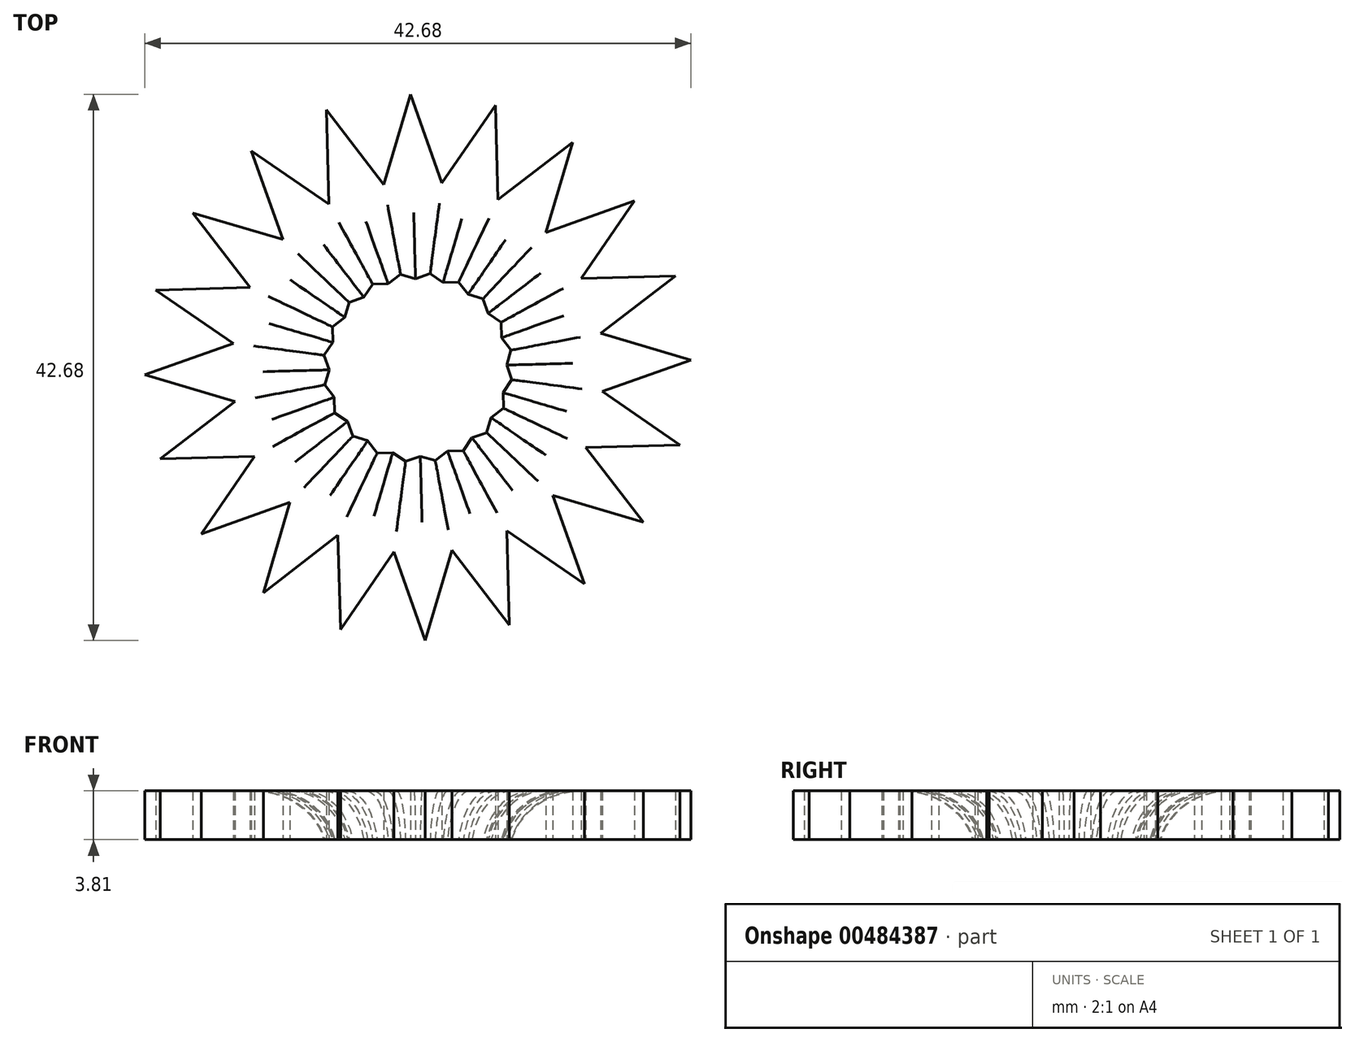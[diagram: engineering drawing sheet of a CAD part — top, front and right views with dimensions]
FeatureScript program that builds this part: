
annotation { "Feature Type Name" : "Feature", "Feature Type Description" : "" }
export const myFeature = defineFeature(function(context is Context, id is Id, definition is map)
    precondition{}
    {
        {
            var Q0;
            Q0=qCreatedBy(makeId("Top.planeOp"),FACE);
            var sketch = newSketch(context, id + "F0", { "sketchPlane" : qUnion([Q0])});
            skCircle(sketch, "E0.cCircle", {"center": v(0, 0) * mm, "radius": 21.09 * mm, "construction": true});
            skLineSegment(sketch, "E0.0", {"start": v(-20.48, 6.04) * mm, "end": v(-17.6, 12.08) * mm});
            skLineSegment(sketch, "E0.1", {"start": v(-17.6, 12.08) * mm, "end": v(-13.01, 16.93) * mm});
            skLineSegment(sketch, "E0.2", {"start": v(-13.01, 16.93) * mm, "end": v(-7.15, 20.12) * mm});
            skLineSegment(sketch, "E0.3", {"start": v(-7.15, 20.12) * mm, "end": v(-0.58, 21.34) * mm});
            skLineSegment(sketch, "E0.4", {"start": v(-0.58, 21.34) * mm, "end": v(6.04, 20.48) * mm});
            skLineSegment(sketch, "E0.5", {"start": v(6.04, 20.48) * mm, "end": v(12.08, 17.6) * mm});
            skLineSegment(sketch, "E0.6", {"start": v(12.08, 17.6) * mm, "end": v(16.93, 13.01) * mm});
            skLineSegment(sketch, "E0.7", {"start": v(16.93, 13.01) * mm, "end": v(20.12, 7.15) * mm});
            skLineSegment(sketch, "E0.8", {"start": v(20.12, 7.15) * mm, "end": v(21.34, 0.58) * mm});
            skLineSegment(sketch, "E0.9", {"start": v(21.34, 0.58) * mm, "end": v(20.48, -6.04) * mm});
            skLineSegment(sketch, "E0.10", {"start": v(20.48, -6.04) * mm, "end": v(17.6, -12.08) * mm});
            skLineSegment(sketch, "E0.11", {"start": v(17.6, -12.08) * mm, "end": v(13.01, -16.93) * mm});
            skLineSegment(sketch, "E0.12", {"start": v(13.01, -16.93) * mm, "end": v(7.15, -20.12) * mm});
            skLineSegment(sketch, "E0.13", {"start": v(7.15, -20.12) * mm, "end": v(0.58, -21.34) * mm});
            skLineSegment(sketch, "E0.14", {"start": v(0.58, -21.34) * mm, "end": v(-6.04, -20.48) * mm});
            skLineSegment(sketch, "E0.15", {"start": v(-6.04, -20.48) * mm, "end": v(-12.08, -17.6) * mm});
            skLineSegment(sketch, "E0.16", {"start": v(-12.08, -17.6) * mm, "end": v(-16.93, -13.01) * mm});
            skLineSegment(sketch, "E0.17", {"start": v(-16.93, -13.01) * mm, "end": v(-20.12, -7.15) * mm});
            skLineSegment(sketch, "E0.18", {"start": v(-20.12, -7.15) * mm, "end": v(-21.34, -0.58) * mm});
            skLineSegment(sketch, "E0.19", {"start": v(-21.34, -0.58) * mm, "end": v(-20.48, 6.04) * mm});
            skLineSegment(sketch, "E1", {"start": v(-12.08, -17.6) * mm, "end": v(-0.58, 21.34) * mm});
            skLineSegment(sketch, "E2", {"start": v(-0.58, 21.34) * mm, "end": v(13.01, -16.93) * mm});
            skLineSegment(sketch, "E3", {"start": v(13.01, -16.93) * mm, "end": v(-20.48, 6.04) * mm});
            skLineSegment(sketch, "E4", {"start": v(-16.93, -13.01) * mm, "end": v(6.04, 20.48) * mm});
            skLineSegment(sketch, "E5", {"start": v(6.04, 20.48) * mm, "end": v(7.15, -20.12) * mm});
            skLineSegment(sketch, "E6", {"start": v(7.15, -20.12) * mm, "end": v(-17.6, 12.08) * mm});
            skLineSegment(sketch, "E7", {"start": v(-17.6, 12.08) * mm, "end": v(21.34, 0.58) * mm});
            skLineSegment(sketch, "E8", {"start": v(21.34, 0.58) * mm, "end": v(-16.93, -13.01) * mm});
            skLineSegment(sketch, "E9", {"start": v(-20.48, 6.04) * mm, "end": v(20.12, 7.15) * mm});
            skLineSegment(sketch, "E10", {"start": v(20.12, 7.15) * mm, "end": v(-12.08, -17.6) * mm});
            skLineSegment(sketch, "E11", {"start": v(-20.12, -7.15) * mm, "end": v(12.08, 17.6) * mm});
            skLineSegment(sketch, "E12", {"start": v(-13.01, 16.93) * mm, "end": v(20.48, -6.04) * mm});
            skLineSegment(sketch, "E13", {"start": v(20.48, -6.04) * mm, "end": v(-20.12, -7.15) * mm});
            skLineSegment(sketch, "E14", {"start": v(-21.34, -0.58) * mm, "end": v(16.93, 13.01) * mm});
            skLineSegment(sketch, "E15", {"start": v(-7.15, 20.12) * mm, "end": v(17.6, -12.08) * mm});
            skLineSegment(sketch, "E16", {"start": v(17.6, -12.08) * mm, "end": v(-21.34, -0.58) * mm});
            skLineSegment(sketch, "E17", {"start": v(-6.04, -20.48) * mm, "end": v(16.93, 13.01) * mm});
            skLineSegment(sketch, "E18", {"start": v(0.58, -21.34) * mm, "end": v(-13.01, 16.93) * mm});
            skLineSegment(sketch, "E19", {"start": v(-6.04, -20.48) * mm, "end": v(-7.15, 20.12) * mm});
            skLineSegment(sketch, "E20", {"start": v(12.08, 17.6) * mm, "end": v(0.58, -21.34) * mm});
            skSolve(sketch);
        }
        {
            var Q0;
            {var subQ1=sQuery(id+"F0.wireOp",EDGE,"E1");var subQ3=sQuery(id+"F0.wireOp",EDGE,"E8");var subQ4=makeQuery(id+"F0.imprint","INTERSECT",VERTEX,{"derivedFrom":[subQ1,subQ3]});Q0=makeQuery(id+"F0.imprint","IMPRINT",FACE,{"disambiguationData":[TD([[makeQuery(id+"F0.imprint","IMPRINT",EDGE,{"disambiguationData":[TD([[subQ4,1.0]])],"derivedFrom":subQ3}),1.0]])]});}
            var Q1;
            {var subQ0=sQuery(id+"F0.wireOp",EDGE,"E8");var subQ1=sQuery(id+"F0.wireOp",EDGE,"E1");var subQ2=makeQuery(id+"F0.imprint","INTERSECT",VERTEX,{"derivedFrom":[subQ1,subQ0]});Q1=makeQuery(id+"F0.imprint","IMPRINT",FACE,{"disambiguationData":[TD([[makeQuery(id+"F0.imprint","IMPRINT",EDGE,{"disambiguationData":[TD([[subQ2,-1.0]])],"derivedFrom":subQ1}),1.0]])]});}
            var Q2;
            {var subQ0=sQuery(id+"F0.wireOp",EDGE,"E12");var subQ1=sQuery(id+"F0.wireOp",EDGE,"E1");var subQ2=makeQuery(id+"F0.imprint","INTERSECT",VERTEX,{"derivedFrom":[subQ1,subQ0]});Q2=makeQuery(id+"F0.imprint","IMPRINT",FACE,{"disambiguationData":[TD([[makeQuery(id+"F0.imprint","IMPRINT",EDGE,{"disambiguationData":[TD([[subQ2,-1.0]])],"derivedFrom":subQ1}),1.0]])]});}
            var Q3;
            {var subQ0=sQuery(id+"F0.wireOp",EDGE,"E2");var subQ5=sQuery(id+"F0.wireOp",EDGE,"E4");var subQ6=makeQuery(id+"F0.imprint","INTERSECT",VERTEX,{"derivedFrom":[subQ0,subQ5]});Q3=makeQuery(id+"F0.imprint","IMPRINT",FACE,{"disambiguationData":[TD([[makeQuery(id+"F0.imprint","IMPRINT",EDGE,{"disambiguationData":[TD([[subQ6,1.0]])],"derivedFrom":subQ5}),1.0]])]});}
            var Q4;
            {var subQ0=sQuery(id+"F0.wireOp",EDGE,"E4");var subQ1=sQuery(id+"F0.wireOp",EDGE,"E2");var subQ2=makeQuery(id+"F0.imprint","INTERSECT",VERTEX,{"derivedFrom":[subQ1,subQ0]});Q4=makeQuery(id+"F0.imprint","IMPRINT",FACE,{"disambiguationData":[TD([[makeQuery(id+"F0.imprint","IMPRINT",EDGE,{"disambiguationData":[TD([[subQ2,-1.0]])],"derivedFrom":subQ1}),1.0]])]});}
            var Q5;
            {var subQ0=sQuery(id+"F0.wireOp",EDGE,"E13");var subQ1=sQuery(id+"F0.wireOp",EDGE,"E2");var subQ2=makeQuery(id+"F0.imprint","INTERSECT",VERTEX,{"derivedFrom":[subQ1,subQ0]});Q5=makeQuery(id+"F0.imprint","IMPRINT",FACE,{"disambiguationData":[TD([[makeQuery(id+"F0.imprint","IMPRINT",EDGE,{"disambiguationData":[TD([[subQ2,-1.0]])],"derivedFrom":subQ1}),1.0]])]});}
            var Q6;
            {var subQ0=sQuery(id+"F0.wireOp",EDGE,"E3");var subQ5=sQuery(id+"F0.wireOp",EDGE,"E5");var subQ6=makeQuery(id+"F0.imprint","INTERSECT",VERTEX,{"derivedFrom":[subQ0,subQ5]});Q6=makeQuery(id+"F0.imprint","IMPRINT",FACE,{"disambiguationData":[TD([[makeQuery(id+"F0.imprint","IMPRINT",EDGE,{"disambiguationData":[TD([[subQ6,1.0]])],"derivedFrom":subQ5}),1.0]])]});}
            var Q7;
            {var subQ0=sQuery(id+"F0.wireOp",EDGE,"E5");var subQ1=sQuery(id+"F0.wireOp",EDGE,"E3");var subQ2=makeQuery(id+"F0.imprint","INTERSECT",VERTEX,{"derivedFrom":[subQ1,subQ0]});Q7=makeQuery(id+"F0.imprint","IMPRINT",FACE,{"disambiguationData":[TD([[makeQuery(id+"F0.imprint","IMPRINT",EDGE,{"disambiguationData":[TD([[subQ2,-1.0]])],"derivedFrom":subQ1}),1.0]])]});}
            var Q8;
            {var subQ0=sQuery(id+"F0.wireOp",EDGE,"E11");var subQ1=sQuery(id+"F0.wireOp",EDGE,"E3");var subQ2=makeQuery(id+"F0.imprint","INTERSECT",VERTEX,{"derivedFrom":[subQ1,subQ0]});Q8=makeQuery(id+"F0.imprint","IMPRINT",FACE,{"disambiguationData":[TD([[makeQuery(id+"F0.imprint","IMPRINT",EDGE,{"disambiguationData":[TD([[subQ2,-1.0]])],"derivedFrom":subQ1}),1.0]])]});}
            var Q9;
            {var subQ3=sQuery(id+"F0.wireOp",EDGE,"E14");var subQ5=sQuery(id+"F0.wireOp",EDGE,"E6");var subQ6=makeQuery(id+"F0.imprint","INTERSECT",VERTEX,{"derivedFrom":[subQ5,subQ3]});Q9=makeQuery(id+"F0.imprint","IMPRINT",FACE,{"disambiguationData":[TD([[makeQuery(id+"F0.imprint","IMPRINT",EDGE,{"disambiguationData":[TD([[subQ6,-1.0]])],"derivedFrom":subQ5}),1.0]])]});}
            var Q10;
            {var subQ0=sQuery(id+"F0.wireOp",EDGE,"E13");var subQ1=sQuery(id+"F0.wireOp",EDGE,"E4");var subQ2=makeQuery(id+"F0.imprint","INTERSECT",VERTEX,{"derivedFrom":[subQ1,subQ0]});Q10=makeQuery(id+"F0.imprint","IMPRINT",FACE,{"disambiguationData":[TD([[makeQuery(id+"F0.imprint","IMPRINT",EDGE,{"disambiguationData":[TD([[subQ2,-1.0]])],"derivedFrom":subQ1}),1.0]])]});}
            var Q11;
            {var subQ0=sQuery(id+"F0.wireOp",EDGE,"E11");var subQ1=sQuery(id+"F0.wireOp",EDGE,"E5");var subQ2=makeQuery(id+"F0.imprint","INTERSECT",VERTEX,{"derivedFrom":[subQ1,subQ0]});Q11=makeQuery(id+"F0.imprint","IMPRINT",FACE,{"disambiguationData":[TD([[makeQuery(id+"F0.imprint","IMPRINT",EDGE,{"disambiguationData":[TD([[subQ2,-1.0]])],"derivedFrom":subQ1}),1.0]])]});}
            var Q12;
            {var subQ0=sQuery(id+"F0.wireOp",EDGE,"E20");var subQ1=sQuery(id+"F0.wireOp",EDGE,"E6");var subQ2=makeQuery(id+"F0.imprint","INTERSECT",VERTEX,{"derivedFrom":[subQ1,subQ0]});Q12=makeQuery(id+"F0.imprint","IMPRINT",FACE,{"disambiguationData":[TD([[makeQuery(id+"F0.imprint","IMPRINT",EDGE,{"disambiguationData":[TD([[subQ2,-1.0]])],"derivedFrom":subQ1}),1.0]])]});}
            var Q13;
            {var subQ1=sQuery(id+"F0.wireOp",EDGE,"E6");var subQ3=sQuery(id+"F0.wireOp",EDGE,"E9");var subQ4=makeQuery(id+"F0.imprint","INTERSECT",VERTEX,{"derivedFrom":[subQ1,subQ3]});Q13=makeQuery(id+"F0.imprint","IMPRINT",FACE,{"disambiguationData":[TD([[makeQuery(id+"F0.imprint","IMPRINT",EDGE,{"disambiguationData":[TD([[subQ4,-1.0]])],"derivedFrom":subQ3}),1.0]])]});}
            var Q14;
            {var subQ0=sQuery(id+"F0.wireOp",EDGE,"E18");var subQ1=sQuery(id+"F0.wireOp",EDGE,"E7");var subQ2=makeQuery(id+"F0.imprint","INTERSECT",VERTEX,{"derivedFrom":[subQ1,subQ0]});Q14=makeQuery(id+"F0.imprint","IMPRINT",FACE,{"disambiguationData":[TD([[makeQuery(id+"F0.imprint","IMPRINT",EDGE,{"disambiguationData":[TD([[subQ2,-1.0]])],"derivedFrom":subQ1}),1.0]])]});}
            var Q15;
            {var subQ0=sQuery(id+"F0.wireOp",EDGE,"E17");var subQ1=sQuery(id+"F0.wireOp",EDGE,"E7");var subQ2=makeQuery(id+"F0.imprint","INTERSECT",VERTEX,{"derivedFrom":[subQ1,subQ0]});Q15=makeQuery(id+"F0.imprint","IMPRINT",FACE,{"disambiguationData":[TD([[makeQuery(id+"F0.imprint","IMPRINT",EDGE,{"disambiguationData":[TD([[subQ2,-1.0]])],"derivedFrom":subQ1}),1.0]])]});}
            var Q16;
            {var subQ1=sQuery(id+"F0.wireOp",EDGE,"E7");var subQ3=sQuery(id+"F0.wireOp",EDGE,"E10");var subQ4=makeQuery(id+"F0.imprint","INTERSECT",VERTEX,{"derivedFrom":[subQ1,subQ3]});Q16=makeQuery(id+"F0.imprint","IMPRINT",FACE,{"disambiguationData":[TD([[makeQuery(id+"F0.imprint","IMPRINT",EDGE,{"disambiguationData":[TD([[subQ4,-1.0]])],"derivedFrom":subQ3}),1.0]])]});}
            var Q17;
            {var subQ0=sQuery(id+"F0.wireOp",EDGE,"E12");var subQ1=sQuery(id+"F0.wireOp",EDGE,"E8");var subQ2=makeQuery(id+"F0.imprint","INTERSECT",VERTEX,{"derivedFrom":[subQ1,subQ0]});Q17=makeQuery(id+"F0.imprint","IMPRINT",FACE,{"disambiguationData":[TD([[makeQuery(id+"F0.imprint","IMPRINT",EDGE,{"disambiguationData":[TD([[subQ2,-1.0]])],"derivedFrom":subQ1}),1.0]])]});}
            var Q18;
            {var subQ0=sQuery(id+"F0.wireOp",EDGE,"E20");var subQ1=sQuery(id+"F0.wireOp",EDGE,"E9");var subQ2=makeQuery(id+"F0.imprint","INTERSECT",VERTEX,{"derivedFrom":[subQ1,subQ0]});Q18=makeQuery(id+"F0.imprint","IMPRINT",FACE,{"disambiguationData":[TD([[makeQuery(id+"F0.imprint","IMPRINT",EDGE,{"disambiguationData":[TD([[subQ2,-1.0]])],"derivedFrom":subQ1}),1.0]])]});}
            var Q19;
            {var subQ0=sQuery(id+"F0.wireOp",EDGE,"E18");var subQ1=sQuery(id+"F0.wireOp",EDGE,"E10");var subQ2=makeQuery(id+"F0.imprint","INTERSECT",VERTEX,{"derivedFrom":[subQ1,subQ0]});Q19=makeQuery(id+"F0.imprint","IMPRINT",FACE,{"disambiguationData":[TD([[makeQuery(id+"F0.imprint","IMPRINT",EDGE,{"disambiguationData":[TD([[subQ2,-1.0]])],"derivedFrom":subQ1}),1.0]])]});}
            var Q20;
            {var subQ0=sQuery(id+"F0.wireOp",EDGE,"E13");var subQ1=sQuery(id+"F0.wireOp",EDGE,"E1");var subQ2=makeQuery(id+"F0.imprint","INTERSECT",VERTEX,{"derivedFrom":[subQ1,subQ0]});Q20=makeQuery(id+"F0.imprint","IMPRINT",FACE,{"disambiguationData":[TD([[makeQuery(id+"F0.imprint","IMPRINT",EDGE,{"disambiguationData":[TD([[subQ2,-1.0]])],"derivedFrom":subQ1}),1.0]])]});}
            var Q21;
            {var subQ0=sQuery(id+"F0.wireOp",EDGE,"E8");var subQ1=sQuery(id+"F0.wireOp",EDGE,"E1");var subQ2=makeQuery(id+"F0.imprint","INTERSECT",VERTEX,{"derivedFrom":[subQ1,subQ0]});Q21=makeQuery(id+"F0.imprint","IMPRINT",FACE,{"disambiguationData":[TD([[makeQuery(id+"F0.imprint","IMPRINT",EDGE,{"disambiguationData":[TD([[subQ2,-1.0]])],"derivedFrom":subQ1}),-1.0]])]});}
            var Q22;
            {var subQ0=sQuery(id+"F0.wireOp",EDGE,"E18");var subQ1=sQuery(id+"F0.wireOp",EDGE,"E8");var subQ2=makeQuery(id+"F0.imprint","INTERSECT",VERTEX,{"derivedFrom":[subQ1,subQ0]});Q22=makeQuery(id+"F0.imprint","IMPRINT",FACE,{"disambiguationData":[TD([[makeQuery(id+"F0.imprint","IMPRINT",EDGE,{"disambiguationData":[TD([[subQ2,-1.0]])],"derivedFrom":subQ1}),1.0]])]});}
            var Q23;
            {var subQ0=sQuery(id+"F0.wireOp",EDGE,"E17");var subQ1=sQuery(id+"F0.wireOp",EDGE,"E6");var subQ2=makeQuery(id+"F0.imprint","INTERSECT",VERTEX,{"derivedFrom":[subQ1,subQ0]});Q23=makeQuery(id+"F0.imprint","IMPRINT",FACE,{"disambiguationData":[TD([[makeQuery(id+"F0.imprint","IMPRINT",EDGE,{"disambiguationData":[TD([[subQ2,-1.0]])],"derivedFrom":subQ1}),1.0]])]});}
            var Q24;
            {var subQ0=sQuery(id+"F0.wireOp",EDGE,"E20");var subQ1=sQuery(id+"F0.wireOp",EDGE,"E3");var subQ2=makeQuery(id+"F0.imprint","INTERSECT",VERTEX,{"derivedFrom":[subQ1,subQ0]});Q24=makeQuery(id+"F0.imprint","IMPRINT",FACE,{"disambiguationData":[TD([[makeQuery(id+"F0.imprint","IMPRINT",EDGE,{"disambiguationData":[TD([[subQ2,-1.0]])],"derivedFrom":subQ1}),1.0]])]});}
            var Q25;
            {var subQ0=sQuery(id+"F0.wireOp",EDGE,"E5");var subQ1=sQuery(id+"F0.wireOp",EDGE,"E3");var subQ2=makeQuery(id+"F0.imprint","INTERSECT",VERTEX,{"derivedFrom":[subQ1,subQ0]});Q25=makeQuery(id+"F0.imprint","IMPRINT",FACE,{"disambiguationData":[TD([[makeQuery(id+"F0.imprint","IMPRINT",EDGE,{"disambiguationData":[TD([[subQ2,-1.0]])],"derivedFrom":subQ1}),-1.0]])]});}
            var Q26;
            {var subQ0=sQuery(id+"F0.wireOp",EDGE,"E13");var subQ1=sQuery(id+"F0.wireOp",EDGE,"E2");var subQ2=makeQuery(id+"F0.imprint","INTERSECT",VERTEX,{"derivedFrom":[subQ1,subQ0]});Q26=makeQuery(id+"F0.imprint","IMPRINT",FACE,{"disambiguationData":[TD([[makeQuery(id+"F0.imprint","IMPRINT",EDGE,{"disambiguationData":[TD([[subQ2,-1.0]])],"derivedFrom":subQ1}),-1.0]])]});}
            var Q27;
            {var subQ0=sQuery(id+"F0.wireOp",EDGE,"E8");var subQ1=sQuery(id+"F0.wireOp",EDGE,"E2");var subQ2=makeQuery(id+"F0.imprint","INTERSECT",VERTEX,{"derivedFrom":[subQ1,subQ0]});Q27=makeQuery(id+"F0.imprint","IMPRINT",FACE,{"disambiguationData":[TD([[makeQuery(id+"F0.imprint","IMPRINT",EDGE,{"disambiguationData":[TD([[subQ2,-1.0]])],"derivedFrom":subQ1}),1.0]])]});}
            var Q28;
            {var subQ0=sQuery(id+"F0.wireOp",EDGE,"E12");var subQ1=sQuery(id+"F0.wireOp",EDGE,"E8");var subQ2=makeQuery(id+"F0.imprint","INTERSECT",VERTEX,{"derivedFrom":[subQ1,subQ0]});Q28=makeQuery(id+"F0.imprint","IMPRINT",FACE,{"disambiguationData":[TD([[makeQuery(id+"F0.imprint","IMPRINT",EDGE,{"disambiguationData":[TD([[subQ2,-1.0]])],"derivedFrom":subQ1}),-1.0]])]});}
            var Q29;
            {var subQ0=sQuery(id+"F0.wireOp",EDGE,"E17");var subQ1=sQuery(id+"F0.wireOp",EDGE,"E7");var subQ2=makeQuery(id+"F0.imprint","INTERSECT",VERTEX,{"derivedFrom":[subQ1,subQ0]});Q29=makeQuery(id+"F0.imprint","IMPRINT",FACE,{"disambiguationData":[TD([[makeQuery(id+"F0.imprint","IMPRINT",EDGE,{"disambiguationData":[TD([[subQ2,-1.0]])],"derivedFrom":subQ1}),-1.0]])]});}
            var Q30;
            {var subQ0=sQuery(id+"F0.wireOp",EDGE,"E20");var subQ1=sQuery(id+"F0.wireOp",EDGE,"E7");var subQ2=makeQuery(id+"F0.imprint","INTERSECT",VERTEX,{"derivedFrom":[subQ1,subQ0]});Q30=makeQuery(id+"F0.imprint","IMPRINT",FACE,{"disambiguationData":[TD([[makeQuery(id+"F0.imprint","IMPRINT",EDGE,{"disambiguationData":[TD([[subQ2,-1.0]])],"derivedFrom":subQ1}),1.0]])]});}
            var Q31;
            {var subQ0=sQuery(id+"F0.wireOp",EDGE,"E14");var subQ1=sQuery(id+"F0.wireOp",EDGE,"E5");var subQ2=makeQuery(id+"F0.imprint","INTERSECT",VERTEX,{"derivedFrom":[subQ1,subQ0]});Q31=makeQuery(id+"F0.imprint","IMPRINT",FACE,{"disambiguationData":[TD([[makeQuery(id+"F0.imprint","IMPRINT",EDGE,{"disambiguationData":[TD([[subQ2,-1.0]])],"derivedFrom":subQ1}),1.0]])]});}
            var Q32;
            {var subQ0=sQuery(id+"F0.wireOp",EDGE,"E11");var subQ1=sQuery(id+"F0.wireOp",EDGE,"E2");var subQ2=makeQuery(id+"F0.imprint","INTERSECT",VERTEX,{"derivedFrom":[subQ1,subQ0]});Q32=makeQuery(id+"F0.imprint","IMPRINT",FACE,{"disambiguationData":[TD([[makeQuery(id+"F0.imprint","IMPRINT",EDGE,{"disambiguationData":[TD([[subQ2,-1.0]])],"derivedFrom":subQ1}),1.0]])]});}
            var Q33;
            {var subQ0=sQuery(id+"F0.wireOp",EDGE,"E4");var subQ1=sQuery(id+"F0.wireOp",EDGE,"E2");var subQ2=makeQuery(id+"F0.imprint","INTERSECT",VERTEX,{"derivedFrom":[subQ1,subQ0]});Q33=makeQuery(id+"F0.imprint","IMPRINT",FACE,{"disambiguationData":[TD([[makeQuery(id+"F0.imprint","IMPRINT",EDGE,{"disambiguationData":[TD([[subQ2,-1.0]])],"derivedFrom":subQ1}),-1.0]])]});}
            var Q34;
            {var subQ0=sQuery(id+"F0.wireOp",EDGE,"E12");var subQ1=sQuery(id+"F0.wireOp",EDGE,"E1");var subQ2=makeQuery(id+"F0.imprint","INTERSECT",VERTEX,{"derivedFrom":[subQ1,subQ0]});Q34=makeQuery(id+"F0.imprint","IMPRINT",FACE,{"disambiguationData":[TD([[makeQuery(id+"F0.imprint","IMPRINT",EDGE,{"disambiguationData":[TD([[subQ2,-1.0]])],"derivedFrom":subQ1}),-1.0]])]});}
            var Q35;
            {var subQ0=sQuery(id+"F0.wireOp",EDGE,"E7");var subQ1=sQuery(id+"F0.wireOp",EDGE,"E1");var subQ2=makeQuery(id+"F0.imprint","INTERSECT",VERTEX,{"derivedFrom":[subQ1,subQ0]});Q35=makeQuery(id+"F0.imprint","IMPRINT",FACE,{"disambiguationData":[TD([[makeQuery(id+"F0.imprint","IMPRINT",EDGE,{"disambiguationData":[TD([[subQ2,-1.0]])],"derivedFrom":subQ1}),1.0]])]});}
            var Q36;
            {var subQ0=sQuery(id+"F0.wireOp",EDGE,"E18");var subQ1=sQuery(id+"F0.wireOp",EDGE,"E7");var subQ2=makeQuery(id+"F0.imprint","INTERSECT",VERTEX,{"derivedFrom":[subQ1,subQ0]});Q36=makeQuery(id+"F0.imprint","IMPRINT",FACE,{"disambiguationData":[TD([[makeQuery(id+"F0.imprint","IMPRINT",EDGE,{"disambiguationData":[TD([[subQ2,-1.0]])],"derivedFrom":subQ1}),-1.0]])]});}
            var Q37;
            {var subQ0=sQuery(id+"F0.wireOp",EDGE,"E14");var subQ1=sQuery(id+"F0.wireOp",EDGE,"E6");var subQ2=makeQuery(id+"F0.imprint","INTERSECT",VERTEX,{"derivedFrom":[subQ1,subQ0]});Q37=makeQuery(id+"F0.imprint","IMPRINT",FACE,{"disambiguationData":[TD([[makeQuery(id+"F0.imprint","IMPRINT",EDGE,{"disambiguationData":[TD([[subQ2,-1.0]])],"derivedFrom":subQ1}),-1.0]])]});}
            var Q38;
            {var subQ0=sQuery(id+"F0.wireOp",EDGE,"E11");var subQ1=sQuery(id+"F0.wireOp",EDGE,"E3");var subQ2=makeQuery(id+"F0.imprint","INTERSECT",VERTEX,{"derivedFrom":[subQ1,subQ0]});Q38=makeQuery(id+"F0.imprint","IMPRINT",FACE,{"disambiguationData":[TD([[makeQuery(id+"F0.imprint","IMPRINT",EDGE,{"disambiguationData":[TD([[subQ2,-1.0]])],"derivedFrom":subQ1}),-1.0]])]});}
            var Q39;
            {var subQ0=sQuery(id+"F0.wireOp",EDGE,"E4");var subQ1=sQuery(id+"F0.wireOp",EDGE,"E3");var subQ2=makeQuery(id+"F0.imprint","INTERSECT",VERTEX,{"derivedFrom":[subQ1,subQ0]});Q39=makeQuery(id+"F0.imprint","IMPRINT",FACE,{"disambiguationData":[TD([[makeQuery(id+"F0.imprint","IMPRINT",EDGE,{"disambiguationData":[TD([[subQ2,-1.0]])],"derivedFrom":subQ1}),1.0]])]});}
            var Q40;
            {var subQ0=sQuery(id+"F0.wireOp",EDGE,"E10");var subQ1=sQuery(id+"F0.wireOp",EDGE,"E2");var subQ2=makeQuery(id+"F0.imprint","INTERSECT",VERTEX,{"derivedFrom":[subQ1,subQ0]});Q40=makeQuery(id+"F0.imprint","IMPRINT",FACE,{"disambiguationData":[TD([[makeQuery(id+"F0.imprint","IMPRINT",EDGE,{"disambiguationData":[TD([[subQ2,-1.0]])],"derivedFrom":subQ1}),1.0]])]});}
            var Q41;
            {var subQ0=sQuery(id+"F0.wireOp",EDGE,"E12");var subQ1=sQuery(id+"F0.wireOp",EDGE,"E10");var subQ2=makeQuery(id+"F0.imprint","INTERSECT",VERTEX,{"derivedFrom":[subQ1,subQ0]});Q41=makeQuery(id+"F0.imprint","IMPRINT",FACE,{"disambiguationData":[TD([[makeQuery(id+"F0.imprint","IMPRINT",EDGE,{"disambiguationData":[TD([[subQ2,-1.0]])],"derivedFrom":subQ1}),-1.0]])]});}
            var Q42;
            {var subQ0=sQuery(id+"F0.wireOp",EDGE,"E20");var subQ1=sQuery(id+"F0.wireOp",EDGE,"E7");var subQ2=makeQuery(id+"F0.imprint","INTERSECT",VERTEX,{"derivedFrom":[subQ1,subQ0]});Q42=makeQuery(id+"F0.imprint","IMPRINT",FACE,{"disambiguationData":[TD([[makeQuery(id+"F0.imprint","IMPRINT",EDGE,{"disambiguationData":[TD([[subQ2,-1.0]])],"derivedFrom":subQ1}),-1.0]])]});}
            var Q43;
            {var subQ0=sQuery(id+"F0.wireOp",EDGE,"E11");var subQ1=sQuery(id+"F0.wireOp",EDGE,"E2");var subQ2=makeQuery(id+"F0.imprint","INTERSECT",VERTEX,{"derivedFrom":[subQ1,subQ0]});Q43=makeQuery(id+"F0.imprint","IMPRINT",FACE,{"disambiguationData":[TD([[makeQuery(id+"F0.imprint","IMPRINT",EDGE,{"disambiguationData":[TD([[subQ2,-1.0]])],"derivedFrom":subQ1}),-1.0]])]});}
            var Q44;
            {var subQ0=sQuery(id+"F0.wireOp",EDGE,"E12");var subQ1=sQuery(id+"F0.wireOp",EDGE,"E4");var subQ2=makeQuery(id+"F0.imprint","INTERSECT",VERTEX,{"derivedFrom":[subQ1,subQ0]});Q44=makeQuery(id+"F0.imprint","IMPRINT",FACE,{"disambiguationData":[TD([[makeQuery(id+"F0.imprint","IMPRINT",EDGE,{"disambiguationData":[TD([[subQ2,-1.0]])],"derivedFrom":subQ1}),-1.0]])]});}
            var Q45;
            {var subQ0=sQuery(id+"F0.wireOp",EDGE,"E7");var subQ1=sQuery(id+"F0.wireOp",EDGE,"E1");var subQ2=makeQuery(id+"F0.imprint","INTERSECT",VERTEX,{"derivedFrom":[subQ1,subQ0]});Q45=makeQuery(id+"F0.imprint","IMPRINT",FACE,{"disambiguationData":[TD([[makeQuery(id+"F0.imprint","IMPRINT",EDGE,{"disambiguationData":[TD([[subQ2,-1.0]])],"derivedFrom":subQ1}),-1.0]])]});}
            var Q46;
            {var subQ0=sQuery(id+"F0.wireOp",EDGE,"E9");var subQ1=sQuery(id+"F0.wireOp",EDGE,"E1");var subQ2=makeQuery(id+"F0.imprint","INTERSECT",VERTEX,{"derivedFrom":[subQ1,subQ0]});Q46=makeQuery(id+"F0.imprint","IMPRINT",FACE,{"disambiguationData":[TD([[makeQuery(id+"F0.imprint","IMPRINT",EDGE,{"disambiguationData":[TD([[subQ2,-1.0]])],"derivedFrom":subQ1}),1.0]])]});}
            var Q47;
            {var subQ0=sQuery(id+"F0.wireOp",EDGE,"E18");var subQ1=sQuery(id+"F0.wireOp",EDGE,"E9");var subQ2=makeQuery(id+"F0.imprint","INTERSECT",VERTEX,{"derivedFrom":[subQ1,subQ0]});Q47=makeQuery(id+"F0.imprint","IMPRINT",FACE,{"disambiguationData":[TD([[makeQuery(id+"F0.imprint","IMPRINT",EDGE,{"disambiguationData":[TD([[subQ2,-1.0]])],"derivedFrom":subQ1}),-1.0]])]});}
            var Q48;
            {var subQ0=sQuery(id+"F0.wireOp",EDGE,"E11");var subQ1=sQuery(id+"F0.wireOp",EDGE,"E6");var subQ2=makeQuery(id+"F0.imprint","INTERSECT",VERTEX,{"derivedFrom":[subQ1,subQ0]});Q48=makeQuery(id+"F0.imprint","IMPRINT",FACE,{"disambiguationData":[TD([[makeQuery(id+"F0.imprint","IMPRINT",EDGE,{"disambiguationData":[TD([[subQ2,-1.0]])],"derivedFrom":subQ1}),-1.0]])]});}
            var Q49;
            {var subQ0=sQuery(id+"F0.wireOp",EDGE,"E4");var subQ1=sQuery(id+"F0.wireOp",EDGE,"E3");var subQ2=makeQuery(id+"F0.imprint","INTERSECT",VERTEX,{"derivedFrom":[subQ1,subQ0]});Q49=makeQuery(id+"F0.imprint","IMPRINT",FACE,{"disambiguationData":[TD([[makeQuery(id+"F0.imprint","IMPRINT",EDGE,{"disambiguationData":[TD([[subQ2,-1.0]])],"derivedFrom":subQ1}),-1.0]])]});}
            var Q50;
            {var subQ0=sQuery(id+"F0.wireOp",EDGE,"E16");var subQ1=sQuery(id+"F0.wireOp",EDGE,"E1");var subQ2=makeQuery(id+"F0.imprint","INTERSECT",VERTEX,{"derivedFrom":[subQ1,subQ0]});Q50=makeQuery(id+"F0.imprint","IMPRINT",FACE,{"disambiguationData":[TD([[makeQuery(id+"F0.imprint","IMPRINT",EDGE,{"disambiguationData":[TD([[subQ2,-1.0]])],"derivedFrom":subQ1}),1.0]])]});}
            var Q51;
            {var subQ0=sQuery(id+"F0.wireOp",EDGE,"E13");var subQ1=sQuery(id+"F0.wireOp",EDGE,"E1");var subQ2=makeQuery(id+"F0.imprint","INTERSECT",VERTEX,{"derivedFrom":[subQ1,subQ0]});Q51=makeQuery(id+"F0.imprint","IMPRINT",FACE,{"disambiguationData":[TD([[makeQuery(id+"F0.imprint","IMPRINT",EDGE,{"disambiguationData":[TD([[subQ2,-1.0]])],"derivedFrom":subQ1}),-1.0]])]});}
            var Q52;
            {var subQ0=sQuery(id+"F0.wireOp",EDGE,"E18");var subQ1=sQuery(id+"F0.wireOp",EDGE,"E8");var subQ2=makeQuery(id+"F0.imprint","INTERSECT",VERTEX,{"derivedFrom":[subQ1,subQ0]});Q52=makeQuery(id+"F0.imprint","IMPRINT",FACE,{"disambiguationData":[TD([[makeQuery(id+"F0.imprint","IMPRINT",EDGE,{"disambiguationData":[TD([[subQ2,-1.0]])],"derivedFrom":subQ1}),-1.0]])]});}
            var Q53;
            {var subQ0=sQuery(id+"F0.wireOp",EDGE,"E10");var subQ1=sQuery(id+"F0.wireOp",EDGE,"E6");var subQ2=makeQuery(id+"F0.imprint","INTERSECT",VERTEX,{"derivedFrom":[subQ1,subQ0]});Q53=makeQuery(id+"F0.imprint","IMPRINT",FACE,{"disambiguationData":[TD([[makeQuery(id+"F0.imprint","IMPRINT",EDGE,{"disambiguationData":[TD([[subQ2,-1.0]])],"derivedFrom":subQ1}),1.0]])]});}
            var Q54;
            {var subQ0=sQuery(id+"F0.wireOp",EDGE,"E17");var subQ1=sQuery(id+"F0.wireOp",EDGE,"E3");var subQ2=makeQuery(id+"F0.imprint","INTERSECT",VERTEX,{"derivedFrom":[subQ1,subQ0]});Q54=makeQuery(id+"F0.imprint","IMPRINT",FACE,{"disambiguationData":[TD([[makeQuery(id+"F0.imprint","IMPRINT",EDGE,{"disambiguationData":[TD([[subQ2,-1.0]])],"derivedFrom":subQ1}),1.0]])]});}
            var Q55;
            {var subQ0=sQuery(id+"F0.wireOp",EDGE,"E20");var subQ1=sQuery(id+"F0.wireOp",EDGE,"E3");var subQ2=makeQuery(id+"F0.imprint","INTERSECT",VERTEX,{"derivedFrom":[subQ1,subQ0]});Q55=makeQuery(id+"F0.imprint","IMPRINT",FACE,{"disambiguationData":[TD([[makeQuery(id+"F0.imprint","IMPRINT",EDGE,{"disambiguationData":[TD([[subQ2,-1.0]])],"derivedFrom":subQ1}),-1.0]])]});}
            var Q56;
            {var subQ0=sQuery(id+"F0.wireOp",EDGE,"E13");var subQ1=sQuery(id+"F0.wireOp",EDGE,"E5");var subQ2=makeQuery(id+"F0.imprint","INTERSECT",VERTEX,{"derivedFrom":[subQ1,subQ0]});Q56=makeQuery(id+"F0.imprint","IMPRINT",FACE,{"disambiguationData":[TD([[makeQuery(id+"F0.imprint","IMPRINT",EDGE,{"disambiguationData":[TD([[subQ2,-1.0]])],"derivedFrom":subQ1}),-1.0]])]});}
            var Q57;
            {var subQ0=sQuery(id+"F0.wireOp",EDGE,"E8");var subQ1=sQuery(id+"F0.wireOp",EDGE,"E2");var subQ2=makeQuery(id+"F0.imprint","INTERSECT",VERTEX,{"derivedFrom":[subQ1,subQ0]});Q57=makeQuery(id+"F0.imprint","IMPRINT",FACE,{"disambiguationData":[TD([[makeQuery(id+"F0.imprint","IMPRINT",EDGE,{"disambiguationData":[TD([[subQ2,-1.0]])],"derivedFrom":subQ1}),-1.0]])]});}
            var Q58;
            {var subQ0=sQuery(id+"F0.wireOp",EDGE,"E10");var subQ1=sQuery(id+"F0.wireOp",EDGE,"E2");var subQ2=makeQuery(id+"F0.imprint","INTERSECT",VERTEX,{"derivedFrom":[subQ1,subQ0]});Q58=makeQuery(id+"F0.imprint","IMPRINT",FACE,{"disambiguationData":[TD([[makeQuery(id+"F0.imprint","IMPRINT",EDGE,{"disambiguationData":[TD([[subQ2,-1.0]])],"derivedFrom":subQ1}),-1.0]])]});}
            var Q59;
            {var subQ0=sQuery(id+"F0.wireOp",EDGE,"E17");var subQ1=sQuery(id+"F0.wireOp",EDGE,"E2");var subQ2=makeQuery(id+"F0.imprint","INTERSECT",VERTEX,{"derivedFrom":[subQ1,subQ0]});Q59=makeQuery(id+"F0.imprint","IMPRINT",FACE,{"disambiguationData":[TD([[makeQuery(id+"F0.imprint","IMPRINT",EDGE,{"disambiguationData":[TD([[subQ2,-1.0]])],"derivedFrom":subQ1}),1.0]])]});}
            var Q60;
            {var subQ0=sQuery(id+"F0.wireOp",EDGE,"E20");var subQ1=sQuery(id+"F0.wireOp",EDGE,"E12");var subQ2=makeQuery(id+"F0.imprint","INTERSECT",VERTEX,{"derivedFrom":[subQ1,subQ0]});Q60=makeQuery(id+"F0.imprint","IMPRINT",FACE,{"disambiguationData":[TD([[makeQuery(id+"F0.imprint","IMPRINT",EDGE,{"disambiguationData":[TD([[subQ2,-1.0]])],"derivedFrom":subQ1}),-1.0]])]});}
            var Q61;
            {var subQ0=sQuery(id+"F0.wireOp",EDGE,"E9");var subQ1=sQuery(id+"F0.wireOp",EDGE,"E5");var subQ2=makeQuery(id+"F0.imprint","INTERSECT",VERTEX,{"derivedFrom":[subQ1,subQ0]});Q61=makeQuery(id+"F0.imprint","IMPRINT",FACE,{"disambiguationData":[TD([[makeQuery(id+"F0.imprint","IMPRINT",EDGE,{"disambiguationData":[TD([[subQ2,-1.0]])],"derivedFrom":subQ1}),1.0]])]});}
            var Q62;
            {var subQ0=sQuery(id+"F0.wireOp",EDGE,"E14");var subQ1=sQuery(id+"F0.wireOp",EDGE,"E2");var subQ2=makeQuery(id+"F0.imprint","INTERSECT",VERTEX,{"derivedFrom":[subQ1,subQ0]});Q62=makeQuery(id+"F0.imprint","IMPRINT",FACE,{"disambiguationData":[TD([[makeQuery(id+"F0.imprint","IMPRINT",EDGE,{"disambiguationData":[TD([[subQ2,-1.0]])],"derivedFrom":subQ1}),1.0]])]});}
            var Q63;
            {var subQ0=sQuery(id+"F0.wireOp",EDGE,"E7");var subQ1=sQuery(id+"F0.wireOp",EDGE,"E5");var subQ2=makeQuery(id+"F0.imprint","INTERSECT",VERTEX,{"derivedFrom":[subQ1,subQ0]});Q63=makeQuery(id+"F0.imprint","IMPRINT",FACE,{"disambiguationData":[TD([[makeQuery(id+"F0.imprint","IMPRINT",EDGE,{"disambiguationData":[TD([[subQ2,-1.0]])],"derivedFrom":subQ1}),1.0]])]});}
            var Q64;
            {var subQ0=sQuery(id+"F0.wireOp",EDGE,"E9");var subQ1=sQuery(id+"F0.wireOp",EDGE,"E2");var subQ2=makeQuery(id+"F0.imprint","INTERSECT",VERTEX,{"derivedFrom":[subQ1,subQ0]});Q64=makeQuery(id+"F0.imprint","IMPRINT",FACE,{"disambiguationData":[TD([[makeQuery(id+"F0.imprint","IMPRINT",EDGE,{"disambiguationData":[TD([[subQ2,-1.0]])],"derivedFrom":subQ1}),1.0]])]});}
            var Q65;
            {var subQ0=sQuery(id+"F0.wireOp",EDGE,"E14");var subQ1=sQuery(id+"F0.wireOp",EDGE,"E2");var subQ2=makeQuery(id+"F0.imprint","INTERSECT",VERTEX,{"derivedFrom":[subQ1,subQ0]});Q65=makeQuery(id+"F0.imprint","IMPRINT",FACE,{"disambiguationData":[TD([[makeQuery(id+"F0.imprint","IMPRINT",EDGE,{"disambiguationData":[TD([[subQ2,-1.0]])],"derivedFrom":subQ1}),-1.0]])]});}
            var Q66;
            {var subQ0=sQuery(id+"F0.wireOp",EDGE,"E12");var subQ1=sQuery(id+"F0.wireOp",EDGE,"E11");var subQ2=makeQuery(id+"F0.imprint","INTERSECT",VERTEX,{"derivedFrom":[subQ1,subQ0]});Q66=makeQuery(id+"F0.imprint","IMPRINT",FACE,{"disambiguationData":[TD([[makeQuery(id+"F0.imprint","IMPRINT",EDGE,{"disambiguationData":[TD([[subQ2,-1.0]])],"derivedFrom":subQ1}),-1.0]])]});}
            var Q67;
            {var subQ0=sQuery(id+"F0.wireOp",EDGE,"E7");var subQ1=sQuery(id+"F0.wireOp",EDGE,"E4");var subQ2=makeQuery(id+"F0.imprint","INTERSECT",VERTEX,{"derivedFrom":[subQ1,subQ0]});Q67=makeQuery(id+"F0.imprint","IMPRINT",FACE,{"disambiguationData":[TD([[makeQuery(id+"F0.imprint","IMPRINT",EDGE,{"disambiguationData":[TD([[subQ2,-1.0]])],"derivedFrom":subQ1}),-1.0]])]});}
            var Q68;
            {var subQ0=sQuery(id+"F0.wireOp",EDGE,"E9");var subQ1=sQuery(id+"F0.wireOp",EDGE,"E1");var subQ2=makeQuery(id+"F0.imprint","INTERSECT",VERTEX,{"derivedFrom":[subQ1,subQ0]});Q68=makeQuery(id+"F0.imprint","IMPRINT",FACE,{"disambiguationData":[TD([[makeQuery(id+"F0.imprint","IMPRINT",EDGE,{"disambiguationData":[TD([[subQ2,-1.0]])],"derivedFrom":subQ1}),-1.0]])]});}
            var Q69;
            {var subQ0=sQuery(id+"F0.wireOp",EDGE,"E14");var subQ1=sQuery(id+"F0.wireOp",EDGE,"E1");var subQ2=makeQuery(id+"F0.imprint","INTERSECT",VERTEX,{"derivedFrom":[subQ1,subQ0]});Q69=makeQuery(id+"F0.imprint","IMPRINT",FACE,{"disambiguationData":[TD([[makeQuery(id+"F0.imprint","IMPRINT",EDGE,{"disambiguationData":[TD([[subQ2,-1.0]])],"derivedFrom":subQ1}),1.0]])]});}
            var Q70;
            {var subQ0=sQuery(id+"F0.wireOp",EDGE,"E18");var subQ1=sQuery(id+"F0.wireOp",EDGE,"E11");var subQ2=makeQuery(id+"F0.imprint","INTERSECT",VERTEX,{"derivedFrom":[subQ1,subQ0]});Q70=makeQuery(id+"F0.imprint","IMPRINT",FACE,{"disambiguationData":[TD([[makeQuery(id+"F0.imprint","IMPRINT",EDGE,{"disambiguationData":[TD([[subQ2,-1.0]])],"derivedFrom":subQ1}),1.0]])]});}
            var Q71;
            {var subQ0=sQuery(id+"F0.wireOp",EDGE,"E6");var subQ1=sQuery(id+"F0.wireOp",EDGE,"E4");var subQ2=makeQuery(id+"F0.imprint","INTERSECT",VERTEX,{"derivedFrom":[subQ1,subQ0]});Q71=makeQuery(id+"F0.imprint","IMPRINT",FACE,{"disambiguationData":[TD([[makeQuery(id+"F0.imprint","IMPRINT",EDGE,{"disambiguationData":[TD([[subQ2,-1.0]])],"derivedFrom":subQ1}),1.0]])]});}
            var Q72;
            {var subQ0=sQuery(id+"F0.wireOp",EDGE,"E3");var subQ1=sQuery(id+"F0.wireOp",EDGE,"E1");var subQ2=makeQuery(id+"F0.imprint","INTERSECT",VERTEX,{"derivedFrom":[subQ1,subQ0]});Q72=makeQuery(id+"F0.imprint","IMPRINT",FACE,{"disambiguationData":[TD([[makeQuery(id+"F0.imprint","IMPRINT",EDGE,{"disambiguationData":[TD([[subQ2,-1.0]])],"derivedFrom":subQ1}),1.0]])]});}
            var Q73;
            {var subQ0=sQuery(id+"F0.wireOp",EDGE,"E16");var subQ1=sQuery(id+"F0.wireOp",EDGE,"E1");var subQ2=makeQuery(id+"F0.imprint","INTERSECT",VERTEX,{"derivedFrom":[subQ1,subQ0]});Q73=makeQuery(id+"F0.imprint","IMPRINT",FACE,{"disambiguationData":[TD([[makeQuery(id+"F0.imprint","IMPRINT",EDGE,{"disambiguationData":[TD([[subQ2,-1.0]])],"derivedFrom":subQ1}),-1.0]])]});}
            var Q74;
            {var subQ0=sQuery(id+"F0.wireOp",EDGE,"E18");var subQ1=sQuery(id+"F0.wireOp",EDGE,"E13");var subQ2=makeQuery(id+"F0.imprint","INTERSECT",VERTEX,{"derivedFrom":[subQ1,subQ0]});Q74=makeQuery(id+"F0.imprint","IMPRINT",FACE,{"disambiguationData":[TD([[makeQuery(id+"F0.imprint","IMPRINT",EDGE,{"disambiguationData":[TD([[subQ2,-1.0]])],"derivedFrom":subQ1}),-1.0]])]});}
            var Q75;
            {var subQ0=sQuery(id+"F0.wireOp",EDGE,"E8");var subQ1=sQuery(id+"F0.wireOp",EDGE,"E6");var subQ2=makeQuery(id+"F0.imprint","INTERSECT",VERTEX,{"derivedFrom":[subQ1,subQ0]});Q75=makeQuery(id+"F0.imprint","IMPRINT",FACE,{"disambiguationData":[TD([[makeQuery(id+"F0.imprint","IMPRINT",EDGE,{"disambiguationData":[TD([[subQ2,-1.0]])],"derivedFrom":subQ1}),1.0]])]});}
            var Q76;
            {var subQ0=sQuery(id+"F0.wireOp",EDGE,"E10");var subQ1=sQuery(id+"F0.wireOp",EDGE,"E3");var subQ2=makeQuery(id+"F0.imprint","INTERSECT",VERTEX,{"derivedFrom":[subQ1,subQ0]});Q76=makeQuery(id+"F0.imprint","IMPRINT",FACE,{"disambiguationData":[TD([[makeQuery(id+"F0.imprint","IMPRINT",EDGE,{"disambiguationData":[TD([[subQ2,-1.0]])],"derivedFrom":subQ1}),1.0]])]});}
            var Q77;
            {var subQ0=sQuery(id+"F0.wireOp",EDGE,"E17");var subQ1=sQuery(id+"F0.wireOp",EDGE,"E3");var subQ2=makeQuery(id+"F0.imprint","INTERSECT",VERTEX,{"derivedFrom":[subQ1,subQ0]});Q77=makeQuery(id+"F0.imprint","IMPRINT",FACE,{"disambiguationData":[TD([[makeQuery(id+"F0.imprint","IMPRINT",EDGE,{"disambiguationData":[TD([[subQ2,-1.0]])],"derivedFrom":subQ1}),-1.0]])]});}
            var Q78;
            {var subQ0=sQuery(id+"F0.wireOp",EDGE,"E20");var subQ1=sQuery(id+"F0.wireOp",EDGE,"E13");var subQ2=makeQuery(id+"F0.imprint","INTERSECT",VERTEX,{"derivedFrom":[subQ1,subQ0]});Q78=makeQuery(id+"F0.imprint","IMPRINT",FACE,{"disambiguationData":[TD([[makeQuery(id+"F0.imprint","IMPRINT",EDGE,{"disambiguationData":[TD([[subQ2,-1.0]])],"derivedFrom":subQ1}),1.0]])]});}
            var Q79;
            {var subQ0=sQuery(id+"F0.wireOp",EDGE,"E8");var subQ1=sQuery(id+"F0.wireOp",EDGE,"E5");var subQ2=makeQuery(id+"F0.imprint","INTERSECT",VERTEX,{"derivedFrom":[subQ1,subQ0]});Q79=makeQuery(id+"F0.imprint","IMPRINT",FACE,{"disambiguationData":[TD([[makeQuery(id+"F0.imprint","IMPRINT",EDGE,{"disambiguationData":[TD([[subQ2,-1.0]])],"derivedFrom":subQ1}),-1.0]])]});}
            var Q80;
            {var subQ0=sQuery(id+"F0.wireOp",EDGE,"E10");var subQ1=sQuery(id+"F0.wireOp",EDGE,"E5");var subQ2=makeQuery(id+"F0.imprint","INTERSECT",VERTEX,{"derivedFrom":[subQ1,subQ0]});Q80=makeQuery(id+"F0.imprint","IMPRINT",FACE,{"disambiguationData":[TD([[makeQuery(id+"F0.imprint","IMPRINT",EDGE,{"disambiguationData":[TD([[subQ2,-1.0]])],"derivedFrom":subQ1}),-1.0]])]});}
            var Q81;
            {var subQ0=sQuery(id+"F0.wireOp",EDGE,"E20");var subQ1=sQuery(id+"F0.wireOp",EDGE,"E2");var subQ2=makeQuery(id+"F0.imprint","INTERSECT",VERTEX,{"derivedFrom":[subQ1,subQ0]});Q81=makeQuery(id+"F0.imprint","IMPRINT",FACE,{"disambiguationData":[TD([[makeQuery(id+"F0.imprint","IMPRINT",EDGE,{"disambiguationData":[TD([[subQ2,-1.0]])],"derivedFrom":subQ1}),1.0]])]});}
            var Q82;
            {var subQ0=sQuery(id+"F0.wireOp",EDGE,"E12");var subQ1=sQuery(id+"F0.wireOp",EDGE,"E5");var subQ2=makeQuery(id+"F0.imprint","INTERSECT",VERTEX,{"derivedFrom":[subQ1,subQ0]});Q82=makeQuery(id+"F0.imprint","IMPRINT",FACE,{"disambiguationData":[TD([[makeQuery(id+"F0.imprint","IMPRINT",EDGE,{"disambiguationData":[TD([[subQ2,-1.0]])],"derivedFrom":subQ1}),1.0]])]});}
            var Q83;
            {var subQ0=sQuery(id+"F0.wireOp",EDGE,"E7");var subQ1=sQuery(id+"F0.wireOp",EDGE,"E2");var subQ2=makeQuery(id+"F0.imprint","INTERSECT",VERTEX,{"derivedFrom":[subQ1,subQ0]});Q83=makeQuery(id+"F0.imprint","IMPRINT",FACE,{"disambiguationData":[TD([[makeQuery(id+"F0.imprint","IMPRINT",EDGE,{"disambiguationData":[TD([[subQ2,-1.0]])],"derivedFrom":subQ1}),1.0]])]});}
            var Q84;
            {var subQ0=sQuery(id+"F0.wireOp",EDGE,"E9");var subQ1=sQuery(id+"F0.wireOp",EDGE,"E2");var subQ2=makeQuery(id+"F0.imprint","INTERSECT",VERTEX,{"derivedFrom":[subQ1,subQ0]});Q84=makeQuery(id+"F0.imprint","IMPRINT",FACE,{"disambiguationData":[TD([[makeQuery(id+"F0.imprint","IMPRINT",EDGE,{"disambiguationData":[TD([[subQ2,-1.0]])],"derivedFrom":subQ1}),-1.0]])]});}
            var Q85;
            {var subQ0=sQuery(id+"F0.wireOp",EDGE,"E12");var subQ1=sQuery(id+"F0.wireOp",EDGE,"E9");var subQ2=makeQuery(id+"F0.imprint","INTERSECT",VERTEX,{"derivedFrom":[subQ1,subQ0]});Q85=makeQuery(id+"F0.imprint","IMPRINT",FACE,{"disambiguationData":[TD([[makeQuery(id+"F0.imprint","IMPRINT",EDGE,{"disambiguationData":[TD([[subQ2,-1.0]])],"derivedFrom":subQ1}),1.0]])]});}
            var Q86;
            {var subQ0=sQuery(id+"F0.wireOp",EDGE,"E11");var subQ1=sQuery(id+"F0.wireOp",EDGE,"E7");var subQ2=makeQuery(id+"F0.imprint","INTERSECT",VERTEX,{"derivedFrom":[subQ1,subQ0]});Q86=makeQuery(id+"F0.imprint","IMPRINT",FACE,{"disambiguationData":[TD([[makeQuery(id+"F0.imprint","IMPRINT",EDGE,{"disambiguationData":[TD([[subQ2,-1.0]])],"derivedFrom":subQ1}),1.0]])]});}
            var Q87;
            {var subQ0=sQuery(id+"F0.wireOp",EDGE,"E9");var subQ1=sQuery(id+"F0.wireOp",EDGE,"E4");var subQ2=makeQuery(id+"F0.imprint","INTERSECT",VERTEX,{"derivedFrom":[subQ1,subQ0]});Q87=makeQuery(id+"F0.imprint","IMPRINT",FACE,{"disambiguationData":[TD([[makeQuery(id+"F0.imprint","IMPRINT",EDGE,{"disambiguationData":[TD([[subQ2,-1.0]])],"derivedFrom":subQ1}),-1.0]])]});}
            var Q88;
            {var subQ0=sQuery(id+"F0.wireOp",EDGE,"E14");var subQ1=sQuery(id+"F0.wireOp",EDGE,"E1");var subQ2=makeQuery(id+"F0.imprint","INTERSECT",VERTEX,{"derivedFrom":[subQ1,subQ0]});Q88=makeQuery(id+"F0.imprint","IMPRINT",FACE,{"disambiguationData":[TD([[makeQuery(id+"F0.imprint","IMPRINT",EDGE,{"disambiguationData":[TD([[subQ2,-1.0]])],"derivedFrom":subQ1}),-1.0]])]});}
            var Q89;
            {var subQ0=sQuery(id+"F0.wireOp",EDGE,"E11");var subQ1=sQuery(id+"F0.wireOp",EDGE,"E1");var subQ2=makeQuery(id+"F0.imprint","INTERSECT",VERTEX,{"derivedFrom":[subQ1,subQ0]});Q89=makeQuery(id+"F0.imprint","IMPRINT",FACE,{"disambiguationData":[TD([[makeQuery(id+"F0.imprint","IMPRINT",EDGE,{"disambiguationData":[TD([[subQ2,-1.0]])],"derivedFrom":subQ1}),1.0]])]});}
            var Q90;
            {var subQ0=sQuery(id+"F0.wireOp",EDGE,"E18");var subQ1=sQuery(id+"F0.wireOp",EDGE,"E4");var subQ2=makeQuery(id+"F0.imprint","INTERSECT",VERTEX,{"derivedFrom":[subQ1,subQ0]});Q90=makeQuery(id+"F0.imprint","IMPRINT",FACE,{"disambiguationData":[TD([[makeQuery(id+"F0.imprint","IMPRINT",EDGE,{"disambiguationData":[TD([[subQ2,-1.0]])],"derivedFrom":subQ1}),1.0]])]});}
            var Q91;
            {var subQ0=sQuery(id+"F0.wireOp",EDGE,"E6");var subQ1=sQuery(id+"F0.wireOp",EDGE,"E1");var subQ2=makeQuery(id+"F0.imprint","INTERSECT",VERTEX,{"derivedFrom":[subQ1,subQ0]});Q91=makeQuery(id+"F0.imprint","IMPRINT",FACE,{"disambiguationData":[TD([[makeQuery(id+"F0.imprint","IMPRINT",EDGE,{"disambiguationData":[TD([[subQ2,-1.0]])],"derivedFrom":subQ1}),1.0]])]});}
            var Q92;
            {var subQ0=sQuery(id+"F0.wireOp",EDGE,"E3");var subQ1=sQuery(id+"F0.wireOp",EDGE,"E1");var subQ2=makeQuery(id+"F0.imprint","INTERSECT",VERTEX,{"derivedFrom":[subQ1,subQ0]});Q92=makeQuery(id+"F0.imprint","IMPRINT",FACE,{"disambiguationData":[TD([[makeQuery(id+"F0.imprint","IMPRINT",EDGE,{"disambiguationData":[TD([[subQ2,-1.0]])],"derivedFrom":subQ1}),-1.0]])]});}
            var Q93;
            {var subQ0=sQuery(id+"F0.wireOp",EDGE,"E18");var subQ1=sQuery(id+"F0.wireOp",EDGE,"E3");var subQ2=makeQuery(id+"F0.imprint","INTERSECT",VERTEX,{"derivedFrom":[subQ1,subQ0]});Q93=makeQuery(id+"F0.imprint","IMPRINT",FACE,{"disambiguationData":[TD([[makeQuery(id+"F0.imprint","IMPRINT",EDGE,{"disambiguationData":[TD([[subQ2,-1.0]])],"derivedFrom":subQ1}),1.0]])]});}
            var Q94;
            {var subQ0=sQuery(id+"F0.wireOp",EDGE,"E13");var subQ1=sQuery(id+"F0.wireOp",EDGE,"E6");var subQ2=makeQuery(id+"F0.imprint","INTERSECT",VERTEX,{"derivedFrom":[subQ1,subQ0]});Q94=makeQuery(id+"F0.imprint","IMPRINT",FACE,{"disambiguationData":[TD([[makeQuery(id+"F0.imprint","IMPRINT",EDGE,{"disambiguationData":[TD([[subQ2,-1.0]])],"derivedFrom":subQ1}),1.0]])]});}
            var Q95;
            {var subQ0=sQuery(id+"F0.wireOp",EDGE,"E8");var subQ1=sQuery(id+"F0.wireOp",EDGE,"E3");var subQ2=makeQuery(id+"F0.imprint","INTERSECT",VERTEX,{"derivedFrom":[subQ1,subQ0]});Q95=makeQuery(id+"F0.imprint","IMPRINT",FACE,{"disambiguationData":[TD([[makeQuery(id+"F0.imprint","IMPRINT",EDGE,{"disambiguationData":[TD([[subQ2,-1.0]])],"derivedFrom":subQ1}),1.0]])]});}
            var Q96;
            {var subQ0=sQuery(id+"F0.wireOp",EDGE,"E10");var subQ1=sQuery(id+"F0.wireOp",EDGE,"E3");var subQ2=makeQuery(id+"F0.imprint","INTERSECT",VERTEX,{"derivedFrom":[subQ1,subQ0]});Q96=makeQuery(id+"F0.imprint","IMPRINT",FACE,{"disambiguationData":[TD([[makeQuery(id+"F0.imprint","IMPRINT",EDGE,{"disambiguationData":[TD([[subQ2,-1.0]])],"derivedFrom":subQ1}),-1.0]])]});}
            var Q97;
            {var subQ0=sQuery(id+"F0.wireOp",EDGE,"E13");var subQ1=sQuery(id+"F0.wireOp",EDGE,"E10");var subQ2=makeQuery(id+"F0.imprint","INTERSECT",VERTEX,{"derivedFrom":[subQ1,subQ0]});Q97=makeQuery(id+"F0.imprint","IMPRINT",FACE,{"disambiguationData":[TD([[makeQuery(id+"F0.imprint","IMPRINT",EDGE,{"disambiguationData":[TD([[subQ2,-1.0]])],"derivedFrom":subQ1}),1.0]])]});}
            var Q98;
            {var subQ0=sQuery(id+"F0.wireOp",EDGE,"E20");var subQ1=sQuery(id+"F0.wireOp",EDGE,"E8");var subQ2=makeQuery(id+"F0.imprint","INTERSECT",VERTEX,{"derivedFrom":[subQ1,subQ0]});Q98=makeQuery(id+"F0.imprint","IMPRINT",FACE,{"disambiguationData":[TD([[makeQuery(id+"F0.imprint","IMPRINT",EDGE,{"disambiguationData":[TD([[subQ2,-1.0]])],"derivedFrom":subQ1}),1.0]])]});}
            var Q99;
            {var subQ0=sQuery(id+"F0.wireOp",EDGE,"E17");var subQ1=sQuery(id+"F0.wireOp",EDGE,"E2");var subQ2=makeQuery(id+"F0.imprint","INTERSECT",VERTEX,{"derivedFrom":[subQ1,subQ0]});Q99=makeQuery(id+"F0.imprint","IMPRINT",FACE,{"disambiguationData":[TD([[makeQuery(id+"F0.imprint","IMPRINT",EDGE,{"disambiguationData":[TD([[subQ2,-1.0]])],"derivedFrom":subQ1}),-1.0]])]});}
            extrude(context, id + "F1", {"entities" : qUnion([Q0, Q1, Q2, Q3, Q4, Q5, Q6, Q7, Q8, Q9, Q10, Q11, Q12, Q13, Q14, Q15, Q16, Q17, Q18, Q19, Q20, Q21, Q22, Q23, Q24, Q25, Q26, Q27, Q28, Q29, Q30, Q31, Q32, Q33, Q34, Q35, Q36, Q37, Q38, Q39, Q40, Q41, Q42, Q43, Q44, Q45, Q46, Q47, Q48, Q49, Q50, Q51, Q52, Q53, Q54, Q55, Q56, Q57, Q58, Q59, Q60, Q61, Q62, Q63, Q64, Q65, Q66, Q67, Q68, Q69, Q70, Q71, Q72, Q73, Q74, Q75, Q76, Q77, Q78, Q79, Q80, Q81, Q82, Q83, Q84, Q85, Q86, Q87, Q88, Q89, Q90, Q91, Q92, Q93, Q94, Q95, Q96, Q97, Q98, Q99]), "depth" : 3.8 * mm});
        }
        {
            var Q0;
            {var subQ0=sQuery(id+"F0.wireOp",EDGE,"E9");Q0=makeQuery(id+"F1.opExtrude","CAP_EDGE",EDGE,{"disambiguationData":[OSD([subQ0]),TDD([makeQuery(id+"F0.imprint","IMPRINT",EDGE,{"disambiguationData":[TD([[makeQuery(id+"F0.imprint","INTERSECT",VERTEX,{"derivedFrom":[sQuery(id+"F0.wireOp",EDGE,"E4"),subQ0]}),-1.0]])],"derivedFrom":subQ0})])],"isStart":false});}
            var Q1;
            {var subQ0=sQuery(id+"F0.wireOp",EDGE,"E7");Q1=makeQuery(id+"F1.opExtrude","CAP_EDGE",EDGE,{"disambiguationData":[OSD([subQ0]),TDD([makeQuery(id+"F0.imprint","IMPRINT",EDGE,{"disambiguationData":[TD([[makeQuery(id+"F0.imprint","INTERSECT",VERTEX,{"derivedFrom":[subQ0,sQuery(id+"F0.wireOp",EDGE,"E11")]}),-1.0]])],"derivedFrom":subQ0})])],"isStart":false});}
            var Q2;
            {var subQ0=sQuery(id+"F0.wireOp",EDGE,"E14");Q2=makeQuery(id+"F1.opExtrude","CAP_EDGE",EDGE,{"disambiguationData":[OSD([subQ0]),TDD([makeQuery(id+"F0.imprint","IMPRINT",EDGE,{"disambiguationData":[TD([[makeQuery(id+"F0.imprint","INTERSECT",VERTEX,{"derivedFrom":[sQuery(id+"F0.wireOp",EDGE,"E7"),subQ0]}),-1.0]])],"derivedFrom":subQ0})])],"isStart":false});}
            var Q3;
            {var subQ0=sQuery(id+"F0.wireOp",EDGE,"E12");Q3=makeQuery(id+"F1.opExtrude","CAP_EDGE",EDGE,{"disambiguationData":[OSD([subQ0]),TDD([makeQuery(id+"F0.imprint","IMPRINT",EDGE,{"disambiguationData":[TD([[makeQuery(id+"F0.imprint","INTERSECT",VERTEX,{"derivedFrom":[sQuery(id+"F0.wireOp",EDGE,"E9"),subQ0]}),1.0]])],"derivedFrom":subQ0})])],"isStart":false});}
            var Q4;
            {var subQ0=sQuery(id+"F0.wireOp",EDGE,"E9");Q4=makeQuery(id+"F1.opExtrude","CAP_EDGE",EDGE,{"disambiguationData":[OSD([subQ0]),TDD([makeQuery(id+"F0.imprint","IMPRINT",EDGE,{"disambiguationData":[TD([[makeQuery(id+"F0.imprint","INTERSECT",VERTEX,{"derivedFrom":[subQ0,sQuery(id+"F0.wireOp",EDGE,"E12")]}),-1.0]])],"derivedFrom":subQ0})])],"isStart":false});}
            var Q5;
            {var subQ0=sQuery(id+"F0.wireOp",EDGE,"E15");Q5=makeQuery(id+"F1.opExtrude","CAP_EDGE",EDGE,{"disambiguationData":[OSD([subQ0]),TDD([makeQuery(id+"F0.imprint","IMPRINT",EDGE,{"disambiguationData":[TD([[makeQuery(id+"F0.imprint","INTERSECT",VERTEX,{"derivedFrom":[sQuery(id+"F0.wireOp",EDGE,"E7"),subQ0]}),1.0]])],"derivedFrom":subQ0})])],"isStart":false});}
            var Q6;
            {var subQ0=sQuery(id+"F0.wireOp",EDGE,"E7");Q6=makeQuery(id+"F1.opExtrude","CAP_EDGE",EDGE,{"disambiguationData":[OSD([subQ0]),TDD([makeQuery(id+"F0.imprint","IMPRINT",EDGE,{"disambiguationData":[TD([[makeQuery(id+"F0.imprint","INTERSECT",VERTEX,{"derivedFrom":[sQuery(id+"F0.wireOp",EDGE,"E2"),subQ0]}),1.0]])],"derivedFrom":subQ0})])],"isStart":false});}
            var Q7;
            {var subQ0=sQuery(id+"F0.wireOp",EDGE,"E2");Q7=makeQuery(id+"F1.opExtrude","CAP_EDGE",EDGE,{"disambiguationData":[OSD([subQ0]),TDD([makeQuery(id+"F0.imprint","IMPRINT",EDGE,{"disambiguationData":[TD([[makeQuery(id+"F0.imprint","INTERSECT",VERTEX,{"derivedFrom":[subQ0,sQuery(id+"F0.wireOp",EDGE,"E7")]}),-1.0]])],"derivedFrom":subQ0})])],"isStart":false});}
            var Q8;
            {var subQ0=sQuery(id+"F0.wireOp",EDGE,"E12");Q8=makeQuery(id+"F1.opExtrude","CAP_EDGE",EDGE,{"disambiguationData":[OSD([subQ0]),TDD([makeQuery(id+"F0.imprint","IMPRINT",EDGE,{"disambiguationData":[TD([[makeQuery(id+"F0.imprint","INTERSECT",VERTEX,{"derivedFrom":[sQuery(id+"F0.wireOp",EDGE,"E2"),subQ0]}),-1.0]])],"derivedFrom":subQ0})])],"isStart":false});}
            var Q9;
            {var subQ0=sQuery(id+"F0.wireOp",EDGE,"E5");Q9=makeQuery(id+"F1.opExtrude","CAP_EDGE",EDGE,{"disambiguationData":[OSD([subQ0]),TDD([makeQuery(id+"F0.imprint","IMPRINT",EDGE,{"disambiguationData":[TD([[makeQuery(id+"F0.imprint","INTERSECT",VERTEX,{"derivedFrom":[subQ0,sQuery(id+"F0.wireOp",EDGE,"E12")]}),-1.0]])],"derivedFrom":subQ0})])],"isStart":false});}
            var Q10;
            {var subQ0=sQuery(id+"F0.wireOp",EDGE,"E15");Q10=makeQuery(id+"F1.opExtrude","CAP_EDGE",EDGE,{"disambiguationData":[OSD([subQ0]),TDD([makeQuery(id+"F0.imprint","IMPRINT",EDGE,{"disambiguationData":[TD([[makeQuery(id+"F0.imprint","INTERSECT",VERTEX,{"derivedFrom":[sQuery(id+"F0.wireOp",EDGE,"E5"),subQ0]}),-1.0]])],"derivedFrom":subQ0})])],"isStart":false});}
            var Q11;
            {var subQ0=sQuery(id+"F0.wireOp",EDGE,"E20");Q11=makeQuery(id+"F1.opExtrude","CAP_EDGE",EDGE,{"disambiguationData":[OSD([subQ0]),TDD([makeQuery(id+"F0.imprint","IMPRINT",EDGE,{"disambiguationData":[TD([[makeQuery(id+"F0.imprint","INTERSECT",VERTEX,{"derivedFrom":[sQuery(id+"F0.wireOp",EDGE,"E2"),subQ0]}),1.0]])],"derivedFrom":subQ0})])],"isStart":false});}
            var Q12;
            {var subQ0=sQuery(id+"F0.wireOp",EDGE,"E2");Q12=makeQuery(id+"F1.opExtrude","CAP_EDGE",EDGE,{"disambiguationData":[OSD([subQ0]),TDD([makeQuery(id+"F0.imprint","IMPRINT",EDGE,{"disambiguationData":[TD([[makeQuery(id+"F0.imprint","INTERSECT",VERTEX,{"derivedFrom":[subQ0,sQuery(id+"F0.wireOp",EDGE,"E20")]}),-1.0]])],"derivedFrom":subQ0})])],"isStart":false});}
            var Q13;
            {var subQ0=sQuery(id+"F0.wireOp",EDGE,"E17");Q13=makeQuery(id+"F1.opExtrude","CAP_EDGE",EDGE,{"disambiguationData":[OSD([subQ0]),TDD([makeQuery(id+"F0.imprint","IMPRINT",EDGE,{"disambiguationData":[TD([[makeQuery(id+"F0.imprint","INTERSECT",VERTEX,{"derivedFrom":[sQuery(id+"F0.wireOp",EDGE,"E2"),subQ0]}),1.0]])],"derivedFrom":subQ0})])],"isStart":false});}
            var Q14;
            {var subQ0=sQuery(id+"F0.wireOp",EDGE,"E5");Q14=makeQuery(id+"F1.opExtrude","CAP_EDGE",EDGE,{"disambiguationData":[OSD([subQ0]),TDD([makeQuery(id+"F0.imprint","IMPRINT",EDGE,{"disambiguationData":[TD([[makeQuery(id+"F0.imprint","INTERSECT",VERTEX,{"derivedFrom":[subQ0,sQuery(id+"F0.wireOp",EDGE,"E17")]}),-1.0]])],"derivedFrom":subQ0})])],"isStart":false});}
            var Q15;
            {var subQ0=sQuery(id+"F0.wireOp",EDGE,"E10");Q15=makeQuery(id+"F1.opExtrude","CAP_EDGE",EDGE,{"disambiguationData":[OSD([subQ0]),TDD([makeQuery(id+"F0.imprint","IMPRINT",EDGE,{"disambiguationData":[TD([[makeQuery(id+"F0.imprint","INTERSECT",VERTEX,{"derivedFrom":[sQuery(id+"F0.wireOp",EDGE,"E5"),subQ0]}),-1.0]])],"derivedFrom":subQ0})])],"isStart":false});}
            var Q16;
            {var subQ0=sQuery(id+"F0.wireOp",EDGE,"E20");Q16=makeQuery(id+"F1.opExtrude","CAP_EDGE",EDGE,{"disambiguationData":[OSD([subQ0]),TDD([makeQuery(id+"F0.imprint","IMPRINT",EDGE,{"disambiguationData":[TD([[makeQuery(id+"F0.imprint","INTERSECT",VERTEX,{"derivedFrom":[sQuery(id+"F0.wireOp",EDGE,"E8"),subQ0]}),1.0]])],"derivedFrom":subQ0})])],"isStart":false});}
            var Q17;
            {var subQ0=sQuery(id+"F0.wireOp",EDGE,"E8");Q17=makeQuery(id+"F1.opExtrude","CAP_EDGE",EDGE,{"disambiguationData":[OSD([subQ0]),TDD([makeQuery(id+"F0.imprint","IMPRINT",EDGE,{"disambiguationData":[TD([[makeQuery(id+"F0.imprint","INTERSECT",VERTEX,{"derivedFrom":[subQ0,sQuery(id+"F0.wireOp",EDGE,"E20")]}),-1.0]])],"derivedFrom":subQ0})])],"isStart":false});}
            var Q18;
            {var subQ0=sQuery(id+"F0.wireOp",EDGE,"E17");Q18=makeQuery(id+"F1.opExtrude","CAP_EDGE",EDGE,{"disambiguationData":[OSD([subQ0]),TDD([makeQuery(id+"F0.imprint","IMPRINT",EDGE,{"disambiguationData":[TD([[makeQuery(id+"F0.imprint","INTERSECT",VERTEX,{"derivedFrom":[sQuery(id+"F0.wireOp",EDGE,"E8"),subQ0]}),1.0]])],"derivedFrom":subQ0})])],"isStart":false});}
            var Q19;
            {var subQ0=sQuery(id+"F0.wireOp",EDGE,"E13");Q19=makeQuery(id+"F1.opExtrude","CAP_EDGE",EDGE,{"disambiguationData":[OSD([subQ0]),TDD([makeQuery(id+"F0.imprint","IMPRINT",EDGE,{"disambiguationData":[TD([[makeQuery(id+"F0.imprint","INTERSECT",VERTEX,{"derivedFrom":[sQuery(id+"F0.wireOp",EDGE,"E10"),subQ0]}),1.0]])],"derivedFrom":subQ0})])],"isStart":false});}
            var Q20;
            {var subQ0=sQuery(id+"F0.wireOp",EDGE,"E10");Q20=makeQuery(id+"F1.opExtrude","CAP_EDGE",EDGE,{"disambiguationData":[OSD([subQ0]),TDD([makeQuery(id+"F0.imprint","IMPRINT",EDGE,{"disambiguationData":[TD([[makeQuery(id+"F0.imprint","INTERSECT",VERTEX,{"derivedFrom":[subQ0,sQuery(id+"F0.wireOp",EDGE,"E13")]}),-1.0]])],"derivedFrom":subQ0})])],"isStart":false});}
            var Q21;
            {var subQ0=sQuery(id+"F0.wireOp",EDGE,"E8");Q21=makeQuery(id+"F1.opExtrude","CAP_EDGE",EDGE,{"disambiguationData":[OSD([subQ0]),TDD([makeQuery(id+"F0.imprint","IMPRINT",EDGE,{"disambiguationData":[TD([[makeQuery(id+"F0.imprint","INTERSECT",VERTEX,{"derivedFrom":[sQuery(id+"F0.wireOp",EDGE,"E3"),subQ0]}),1.0]])],"derivedFrom":subQ0})])],"isStart":false});}
            var Q22;
            {var subQ0=sQuery(id+"F0.wireOp",EDGE,"E3");Q22=makeQuery(id+"F1.opExtrude","CAP_EDGE",EDGE,{"disambiguationData":[OSD([subQ0]),TDD([makeQuery(id+"F0.imprint","IMPRINT",EDGE,{"disambiguationData":[TD([[makeQuery(id+"F0.imprint","INTERSECT",VERTEX,{"derivedFrom":[subQ0,sQuery(id+"F0.wireOp",EDGE,"E8")]}),-1.0]])],"derivedFrom":subQ0})])],"isStart":false});}
            var Q23;
            {var subQ0=sQuery(id+"F0.wireOp",EDGE,"E13");Q23=makeQuery(id+"F1.opExtrude","CAP_EDGE",EDGE,{"disambiguationData":[OSD([subQ0]),TDD([makeQuery(id+"F0.imprint","IMPRINT",EDGE,{"disambiguationData":[TD([[makeQuery(id+"F0.imprint","INTERSECT",VERTEX,{"derivedFrom":[sQuery(id+"F0.wireOp",EDGE,"E3"),subQ0]}),-1.0]])],"derivedFrom":subQ0})])],"isStart":false});}
            var Q24;
            {var subQ0=sQuery(id+"F0.wireOp",EDGE,"E6");Q24=makeQuery(id+"F1.opExtrude","CAP_EDGE",EDGE,{"disambiguationData":[OSD([subQ0]),TDD([makeQuery(id+"F0.imprint","IMPRINT",EDGE,{"disambiguationData":[TD([[makeQuery(id+"F0.imprint","INTERSECT",VERTEX,{"derivedFrom":[subQ0,sQuery(id+"F0.wireOp",EDGE,"E13")]}),-1.0]])],"derivedFrom":subQ0})])],"isStart":false});}
            var Q25;
            {var subQ0=sQuery(id+"F0.wireOp",EDGE,"E16");Q25=makeQuery(id+"F1.opExtrude","CAP_EDGE",EDGE,{"disambiguationData":[OSD([subQ0]),TDD([makeQuery(id+"F0.imprint","IMPRINT",EDGE,{"disambiguationData":[TD([[makeQuery(id+"F0.imprint","INTERSECT",VERTEX,{"derivedFrom":[sQuery(id+"F0.wireOp",EDGE,"E8"),subQ0]}),1.0]])],"derivedFrom":subQ0})])],"isStart":false});}
            var Q26;
            {var subQ0=sQuery(id+"F0.wireOp",EDGE,"E16");Q26=makeQuery(id+"F1.opExtrude","CAP_EDGE",EDGE,{"disambiguationData":[OSD([subQ0]),TDD([makeQuery(id+"F0.imprint","IMPRINT",EDGE,{"disambiguationData":[TD([[makeQuery(id+"F0.imprint","INTERSECT",VERTEX,{"derivedFrom":[sQuery(id+"F0.wireOp",EDGE,"E6"),subQ0]}),-1.0]])],"derivedFrom":subQ0})])],"isStart":false});}
            var Q27;
            {var subQ0=sQuery(id+"F0.wireOp",EDGE,"E18");Q27=makeQuery(id+"F1.opExtrude","CAP_EDGE",EDGE,{"disambiguationData":[OSD([subQ0]),TDD([makeQuery(id+"F0.imprint","IMPRINT",EDGE,{"disambiguationData":[TD([[makeQuery(id+"F0.imprint","INTERSECT",VERTEX,{"derivedFrom":[sQuery(id+"F0.wireOp",EDGE,"E3"),subQ0]}),1.0]])],"derivedFrom":subQ0})])],"isStart":false});}
            var Q28;
            {var subQ0=sQuery(id+"F0.wireOp",EDGE,"E3");Q28=makeQuery(id+"F1.opExtrude","CAP_EDGE",EDGE,{"disambiguationData":[OSD([subQ0]),TDD([makeQuery(id+"F0.imprint","IMPRINT",EDGE,{"disambiguationData":[TD([[makeQuery(id+"F0.imprint","INTERSECT",VERTEX,{"derivedFrom":[subQ0,sQuery(id+"F0.wireOp",EDGE,"E18")]}),-1.0]])],"derivedFrom":subQ0})])],"isStart":false});}
            var Q29;
            {var subQ0=sQuery(id+"F0.wireOp",EDGE,"E19");Q29=makeQuery(id+"F1.opExtrude","CAP_EDGE",EDGE,{"disambiguationData":[OSD([subQ0]),TDD([makeQuery(id+"F0.imprint","IMPRINT",EDGE,{"disambiguationData":[TD([[makeQuery(id+"F0.imprint","INTERSECT",VERTEX,{"derivedFrom":[sQuery(id+"F0.wireOp",EDGE,"E3"),subQ0]}),-1.0]])],"derivedFrom":subQ0})])],"isStart":false});}
            var Q30;
            {var subQ0=sQuery(id+"F0.wireOp",EDGE,"E6");Q30=makeQuery(id+"F1.opExtrude","CAP_EDGE",EDGE,{"disambiguationData":[OSD([subQ0]),TDD([makeQuery(id+"F0.imprint","IMPRINT",EDGE,{"disambiguationData":[TD([[makeQuery(id+"F0.imprint","INTERSECT",VERTEX,{"derivedFrom":[sQuery(id+"F0.wireOp",EDGE,"E1"),subQ0]}),1.0]])],"derivedFrom":subQ0})])],"isStart":false});}
            var Q31;
            {var subQ0=sQuery(id+"F0.wireOp",EDGE,"E1");Q31=makeQuery(id+"F1.opExtrude","CAP_EDGE",EDGE,{"disambiguationData":[OSD([subQ0]),TDD([makeQuery(id+"F0.imprint","IMPRINT",EDGE,{"disambiguationData":[TD([[makeQuery(id+"F0.imprint","INTERSECT",VERTEX,{"derivedFrom":[subQ0,sQuery(id+"F0.wireOp",EDGE,"E6")]}),-1.0]])],"derivedFrom":subQ0})])],"isStart":false});}
            var Q32;
            {var subQ0=sQuery(id+"F0.wireOp",EDGE,"E18");Q32=makeQuery(id+"F1.opExtrude","CAP_EDGE",EDGE,{"disambiguationData":[OSD([subQ0]),TDD([makeQuery(id+"F0.imprint","IMPRINT",EDGE,{"disambiguationData":[TD([[makeQuery(id+"F0.imprint","INTERSECT",VERTEX,{"derivedFrom":[sQuery(id+"F0.wireOp",EDGE,"E1"),subQ0]}),-1.0]])],"derivedFrom":subQ0})])],"isStart":false});}
            var Q33;
            {var subQ0=sQuery(id+"F0.wireOp",EDGE,"E4");Q33=makeQuery(id+"F1.opExtrude","CAP_EDGE",EDGE,{"disambiguationData":[OSD([subQ0]),TDD([makeQuery(id+"F0.imprint","IMPRINT",EDGE,{"disambiguationData":[TD([[makeQuery(id+"F0.imprint","INTERSECT",VERTEX,{"derivedFrom":[subQ0,sQuery(id+"F0.wireOp",EDGE,"E18")]}),-1.0]])],"derivedFrom":subQ0})])],"isStart":false});}
            var Q34;
            {var subQ0=sQuery(id+"F0.wireOp",EDGE,"E19");Q34=makeQuery(id+"F1.opExtrude","CAP_EDGE",EDGE,{"disambiguationData":[OSD([subQ0]),TDD([makeQuery(id+"F0.imprint","IMPRINT",EDGE,{"disambiguationData":[TD([[makeQuery(id+"F0.imprint","INTERSECT",VERTEX,{"derivedFrom":[sQuery(id+"F0.wireOp",EDGE,"E4"),subQ0]}),-1.0]])],"derivedFrom":subQ0})])],"isStart":false});}
            var Q35;
            {var subQ0=sQuery(id+"F0.wireOp",EDGE,"E11");Q35=makeQuery(id+"F1.opExtrude","CAP_EDGE",EDGE,{"disambiguationData":[OSD([subQ0]),TDD([makeQuery(id+"F0.imprint","IMPRINT",EDGE,{"disambiguationData":[TD([[makeQuery(id+"F0.imprint","INTERSECT",VERTEX,{"derivedFrom":[sQuery(id+"F0.wireOp",EDGE,"E1"),subQ0]}),1.0]])],"derivedFrom":subQ0})])],"isStart":false});}
            var Q36;
            {var subQ0=sQuery(id+"F0.wireOp",EDGE,"E19");Q36=makeQuery(id+"F1.opExtrude","CAP_EDGE",EDGE,{"disambiguationData":[OSD([subQ0]),TDD([makeQuery(id+"F0.imprint","IMPRINT",EDGE,{"disambiguationData":[TD([[makeQuery(id+"F0.imprint","INTERSECT",VERTEX,{"derivedFrom":[sQuery(id+"F0.wireOp",EDGE,"E4"),subQ0]}),-1.0]])],"derivedFrom":subQ0})])],"isStart":false});}
            var Q37;
            {var subQ0=sQuery(id+"F0.wireOp",EDGE,"E1");Q37=makeQuery(id+"F1.opExtrude","CAP_EDGE",EDGE,{"disambiguationData":[OSD([subQ0]),TDD([makeQuery(id+"F0.imprint","IMPRINT",EDGE,{"disambiguationData":[TD([[makeQuery(id+"F0.imprint","INTERSECT",VERTEX,{"derivedFrom":[subQ0,sQuery(id+"F0.wireOp",EDGE,"E11")]}),-1.0]])],"derivedFrom":subQ0})])],"isStart":false});}
            var Q38;
            {var subQ0=sQuery(id+"F0.wireOp",EDGE,"E14");Q38=makeQuery(id+"F1.opExtrude","CAP_EDGE",EDGE,{"disambiguationData":[OSD([subQ0]),TDD([makeQuery(id+"F0.imprint","IMPRINT",EDGE,{"disambiguationData":[TD([[makeQuery(id+"F0.imprint","INTERSECT",VERTEX,{"derivedFrom":[sQuery(id+"F0.wireOp",EDGE,"E1"),subQ0]}),-1.0]])],"derivedFrom":subQ0})])],"isStart":false});}
            var Q39;
            {var subQ0=sQuery(id+"F0.wireOp",EDGE,"E4");Q39=makeQuery(id+"F1.opExtrude","CAP_EDGE",EDGE,{"disambiguationData":[OSD([subQ0]),TDD([makeQuery(id+"F0.imprint","IMPRINT",EDGE,{"disambiguationData":[TD([[makeQuery(id+"F0.imprint","INTERSECT",VERTEX,{"derivedFrom":[subQ0,sQuery(id+"F0.wireOp",EDGE,"E14")]}),-1.0]])],"derivedFrom":subQ0})])],"isStart":false});}
            var Q40;
            {var subQ0=sQuery(id+"F0.wireOp",EDGE,"E11");Q40=makeQuery(id+"F1.opExtrude","CAP_EDGE",EDGE,{"disambiguationData":[OSD([subQ0]),TDD([makeQuery(id+"F0.imprint","IMPRINT",EDGE,{"disambiguationData":[TD([[makeQuery(id+"F0.imprint","INTERSECT",VERTEX,{"derivedFrom":[sQuery(id+"F0.wireOp",EDGE,"E7"),subQ0]}),1.0]])],"derivedFrom":subQ0})])],"isStart":false});}
            fillet(context, id + "F2", {"entities" : qUnion([Q0, Q1, Q2, Q3, Q4, Q5, Q6, Q7, Q8, Q9, Q10, Q11, Q12, Q13, Q14, Q15, Q16, Q17, Q18, Q19, Q20, Q21, Q22, Q23, Q24, Q25, Q26, Q27, Q28, Q29, Q30, Q31, Q32, Q33, Q34, Q35, Q36, Q37, Q38, Q39, Q40]), "radius" : 5.08 * mm, "tangentPropagation" : true, "allowEdgeOverflow" : false});
        }
    });
